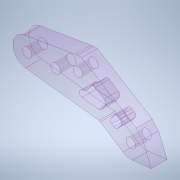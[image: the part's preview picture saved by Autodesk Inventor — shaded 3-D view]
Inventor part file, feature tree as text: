
AUTODESK INVENTOR PART (.ipt)
format: ipt  version: 2020.2 (Build 242310000, 310)  size: 588,800 bytes
history: native  units: mm
features: sketch x15, extrude x15, projected_geometry x8, other x5, hole x5, fillet x4
ambient origin geometry x8: Origin, YZ Plane, XZ Plane, XY Plane, X Axis, Y Axis, Z Axis, Center Point
bodies: Body1 (feature_tree)
feature tree (52):
  other  "ソリッド1"
  sketch  "スケッチ1"
  extrude  "押し出し1"  Depth=5.0mm
  hole  "穴1"  [1 undecoded]
  sketch  "スケッチ2"
  sketch  "スケッチ3"
  sketch  "スケッチ4"
  extrude  "押し出し2"  Depth=6.0mm
  extrude  "押し出し3"  Depth=3.0mm
  hole  "穴2"  [1 undecoded]
  extrude  "押し出し4"  Depth=3.0mm
  sketch  "スケッチ6"
  extrude  "押し出し5"  Depth=3.0mm
  hole  "穴3"  [1 undecoded]
  extrude  "押し出し6"  Depth=3.0mm
  sketch  "スケッチ7"
  sketch  "スケッチ8"
  extrude  "押し出し7"  Depth=19.028919mm
  extrude  "押し出し8"  Depth=3.0mm
  hole  "穴4"  [1 undecoded]
  hole  "穴5"  [1 undecoded]
  extrude  "押し出し9"  Depth=9.0mm
  extrude  "押し出し10"  Depth=9.51446mm
  fillet  "フィレット1"  Radius=5.0mm
  extrude  "押し出し11"  Depth=9.0mm
  fillet  "フィレット2"  Radius=3.0mm
  extrude  "押し出し12"  Depth=9.0mm
  fillet  "フィレット3"  Radius=3.0mm
  sketch  "スケッチ14"
  extrude  "押し出し13"  Depth=14.0mm
  extrude  "押し出し14"  Depth=9.0mm
  extrude  "押し出し15"  Depth=3.0mm
  fillet  "フィレット4"  Radius=3.0mm
  projected_geometry  "投影ループ1"
  projected_geometry  "投影ループ2"
  sketch  "スケッチ5"
  projected_geometry  "投影ループ3"
  projected_geometry  "投影ループ4"
  projected_geometry  "投影ループ5"
  sketch  "スケッチ9"
  sketch  "スケッチ10"
  projected_geometry  "投影ループ6"
  sketch  "スケッチ11"
  projected_geometry  "投影ループ7"
  sketch  "スケッチ12"
  projected_geometry  "投影ループ8"
  sketch  "スケッチ13"
  sketch  "スケッチ15"
  other  "断面エッジを投影1"
  other  "断面エッジを投影2"
  other  "断面エッジを投影3"
  other  "断面エッジを投影4"
note: 5 required parameter values undecoded (feature->parameter linkage not recoverable at this tier; creation-order binding heuristic only, values carry confidence <= 0.55)
